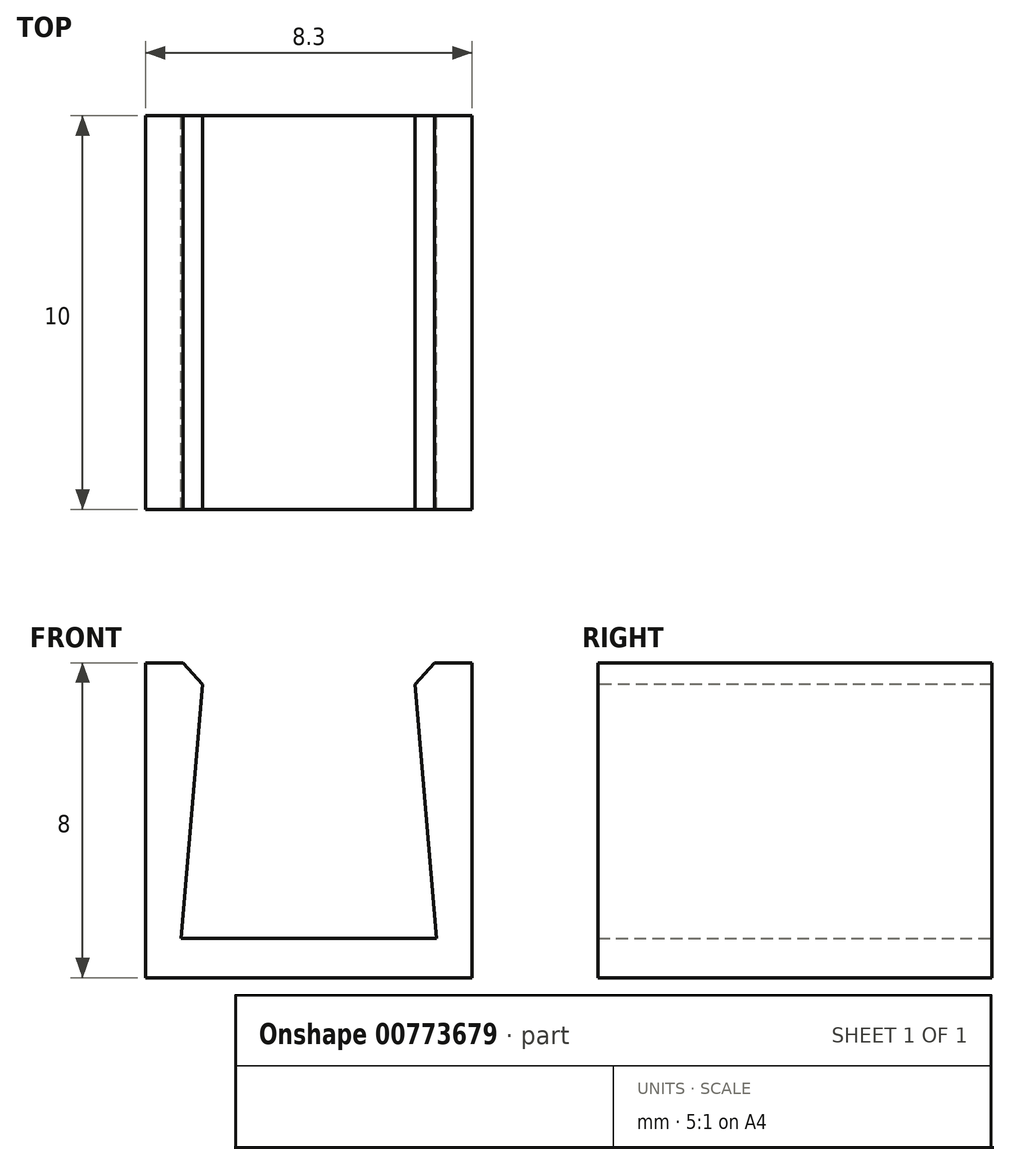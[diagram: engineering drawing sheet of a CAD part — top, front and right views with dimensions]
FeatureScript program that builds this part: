
annotation { "Feature Type Name" : "Feature", "Feature Type Description" : "" }
export const myFeature = defineFeature(function(context is Context, id is Id, definition is map)
    precondition{}
    {
        {
            var Q0;
            Q0=qCreatedBy(makeId("Front.planeOp"),FACE);
            var sketch = newSketch(context, id + "F0", { "sketchPlane" : qUnion([Q0])});
            skLineSegment(sketch, "E0", {"start": v(0, 0) * mm, "end": v(4.15, 0) * mm});
            skLineSegment(sketch, "E1", {"start": v(4.15, 0) * mm, "end": v(4.15, 8) * mm});
            skLineSegment(sketch, "E2", {"start": v(4.15, 8) * mm, "end": v(2.65, 8) * mm});
            skLineSegment(sketch, "E3", {"start": v(2.65, 8) * mm, "end": v(3.25, 1) * mm});
            skLineSegment(sketch, "E4", {"start": v(3.25, 1) * mm, "end": v(0, 1) * mm});
            skLineSegment(sketch, "E5", {"start": v(0, 1) * mm, "end": v(0, 0) * mm});
            skLineSegment(sketch, "E6", {"start": v(0, -3.53) * mm, "end": v(0, 13.14) * mm, "construction": true});
            skLineSegment(sketch, "E7.MirrorCS", {"start": v(0, 0) * mm, "end": v(-4.15, 0) * mm});
            skLineSegment(sketch, "E8.MirrorCS", {"start": v(-4.15, 0) * mm, "end": v(-4.15, 8) * mm});
            skLineSegment(sketch, "E9.MirrorCS", {"start": v(-4.15, 8) * mm, "end": v(-2.65, 8) * mm});
            skLineSegment(sketch, "E10.MirrorCS", {"start": v(-2.65, 8) * mm, "end": v(-3.25, 1) * mm});
            skLineSegment(sketch, "E11.MirrorCS", {"start": v(-3.25, 1) * mm, "end": v(0, 1) * mm});
            skSolve(sketch);
        }
        {
            var Q0;
            Q0=makeQuery(id+"F0.imprint","IMPRINT",FACE,{"disambiguationData":[TD([[makeQuery(id+"F0.imprint","IMPRINT",EDGE,{"derivedFrom":sQuery(id+"F0.wireOp",EDGE,"E0")}),1.0]])]});
            var Q1;
            Q1=makeQuery(id+"F0.imprint","IMPRINT",FACE,{"disambiguationData":[TD([[makeQuery(id+"F0.imprint","IMPRINT",EDGE,{"derivedFrom":sQuery(id+"F0.wireOp",EDGE,"E5")}),-1.0]])]});
            extrude(context, id + "F1", {"entities" : qUnion([Q0, Q1]), "depth" : 10 * mm, "offsetDistance" : 25 * mm});
        }
        {
            var Q0;
            Q0=makeQuery(id+"F1.opExtrude","SWEPT_EDGE",EDGE,{"disambiguationData":[OSD([sQuery(id+"F0.wireOp",EDGE,"E9.MirrorCS"),sQuery(id+"F0.wireOp",EDGE,"E10.MirrorCS")])]});
            var Q1;
            Q1=makeQuery(id+"F1.opExtrude","SWEPT_EDGE",EDGE,{"disambiguationData":[OSD([sQuery(id+"F0.wireOp",EDGE,"E2"),sQuery(id+"F0.wireOp",EDGE,"E3")])]});
            chamfer(context, id + "F2", {"entities" : qUnion([Q0, Q1]), "width" : 0.5 * mm, "tangentPropagation" : true});
        }
    });
